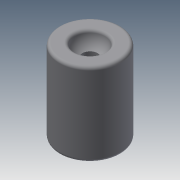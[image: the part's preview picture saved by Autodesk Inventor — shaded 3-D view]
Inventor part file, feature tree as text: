
AUTODESK INVENTOR PART (.ipt)
format: ipt  version: 2015 (Build 190159000, 159)  size: 138,752 bytes
history: native  units: mm
features: sketch x7, extrude x2, revolve x2, fillet x1
ambient origin geometry x8: Origin, YZ Plane, XZ Plane, XY Plane, X Axis, Y Axis, Z Axis, Center Point
bodies: Solid1 (feature_tree)
feature tree (12):
  extrude  "Extrusion1"  Depth=13.5mm TaperAngle=0.0deg
  extrude  "Extrusion2"  Depth=13.5mm TaperAngle=0.0deg
  sketch  "Sketch3"  dims[d6=5.0mm d7=90.0deg]
  revolve  "Revolution1"  Angle=90.0deg
  sketch  "Sketch5"
  revolve  "Revolution2"  Angle=90.0deg
  sketch  "Sketch7"
  fillet  "Fillet1"  Radius=0.5mm
  sketch  "Sketch1"  dims[d0=10.0mm d1=13.5mm d2=0.0mm]
  sketch  "Sketch2"  dims[d3=2.5mm d4=13.5mm d5=0.0mm]
  sketch  "Sketch4"  dims[d8=5.0mm d9=90.0deg d10=0.5mm]
  sketch  "Sketch6"
